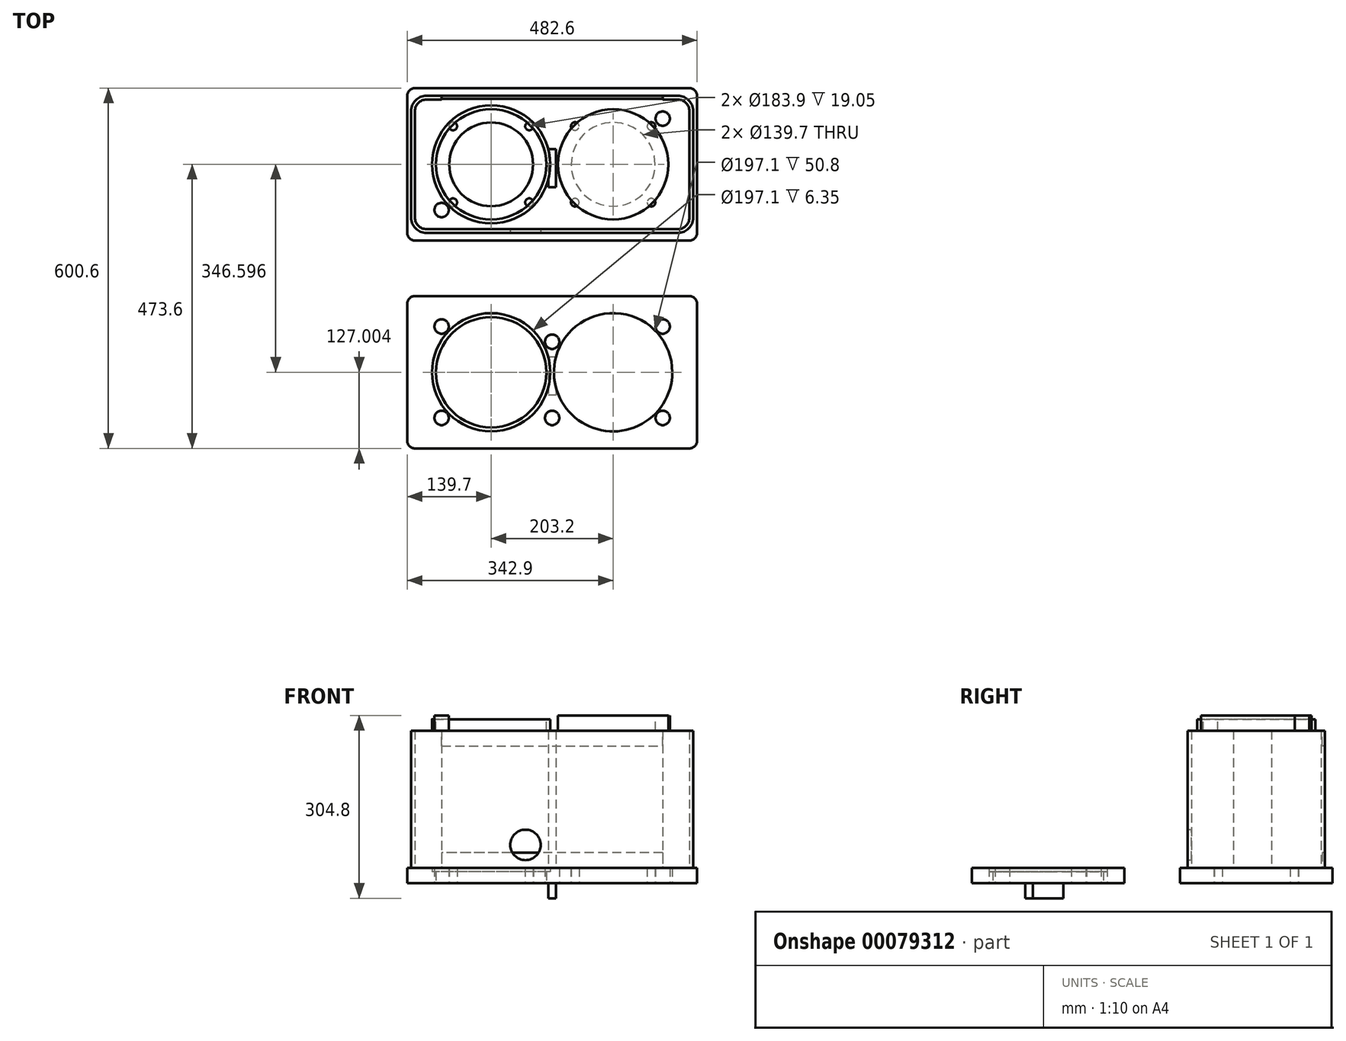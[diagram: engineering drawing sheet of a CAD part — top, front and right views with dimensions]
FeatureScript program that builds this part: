
annotation { "Feature Type Name" : "Feature", "Feature Type Description" : "" }
export const myFeature = defineFeature(function(context is Context, id is Id, definition is map)
    precondition{}
    {
        {
            var Q0;
            Q0=qCreatedBy(makeId("Top.planeOp"),FACE);
            var sketch = newSketch(context, id + "F0", { "sketchPlane" : qUnion([Q0])});
            skLineSegment(sketch, "E0.bottom", {"start": v(241.3, -127) * mm, "end": v(-241.3, -127) * mm});
            skLineSegment(sketch, "E0.top", {"start": v(241.3, 127) * mm, "end": v(-241.3, 127) * mm});
            skLineSegment(sketch, "E0.left", {"start": v(241.3, -127) * mm, "end": v(241.3, 127) * mm});
            skLineSegment(sketch, "E0.right", {"start": v(-241.3, -127) * mm, "end": v(-241.3, 127) * mm});
            skPoint(sketch, "E0.middle", {"position": v(0, 0) * mm});
            skSolve(sketch);
        }
        {
            var Q0;
            Q0=makeQuery(id+"F0.imprint","IMPRINT",FACE,{"disambiguationData":[TD([[makeQuery(id+"F0.imprint","IMPRINT",EDGE,{"derivedFrom":sQuery(id+"F0.wireOp",EDGE,"E0.bottom")}),-1.0]])]});
            extrude(context, id + "F1", {"entities" : qUnion([Q0]), "depth" : 25.4 * mm});
        }
        {
            var Q0;
            Q0=makeQuery(id+"F1.opExtrude","CAP_FACE",FACE,{"disambiguationData":[OSD([sQuery(id+"F0.wireOp",EDGE,"E0.bottom"),sQuery(id+"F0.wireOp",EDGE,"E0.top"),sQuery(id+"F0.wireOp",EDGE,"E0.left"),sQuery(id+"F0.wireOp",EDGE,"E0.right")])],"isStart":false});
            var sketch = newSketch(context, id + "F2", { "sketchPlane" : qUnion([Q0])});
            skLineSegment(sketch, "E1.bottom", {"start": v(209.55, -114.3) * mm, "end": v(-209.55, -114.3) * mm});
            skLineSegment(sketch, "E1.left", {"start": v(234.95, -88.9) * mm, "end": v(234.95, 88.9) * mm});
            skLineSegment(sketch, "E1.right", {"start": v(-234.95, -88.9) * mm, "end": v(-234.95, 88.9) * mm});
            skPoint(sketch, "E1.middle", {"position": v(0, 0) * mm});
            skLineSegment(sketch, "E2.bottom", {"start": v(209.55, -107.95) * mm, "end": v(-209.55, -107.95) * mm});
            skLineSegment(sketch, "E2.left", {"start": v(228.6, -88.9) * mm, "end": v(228.6, 88.9) * mm});
            skLineSegment(sketch, "E2.right", {"start": v(-228.6, -88.9) * mm, "end": v(-228.6, 88.9) * mm});
            skLineSegment(sketch, "E3", {"start": v(-209.55, 114.3) * mm, "end": v(-184.15, 114.3) * mm});
            skLineSegment(sketch, "E4", {"start": v(-209.55, 107.95) * mm, "end": v(-184.14, 107.95) * mm});
            skLineSegment(sketch, "E5", {"start": v(-184.15, 114.3) * mm, "end": v(-184.14, 107.95) * mm});
            skLineSegment(sketch, "E6", {"start": v(209.55, 114.3) * mm, "end": v(184.15, 114.3) * mm});
            skLineSegment(sketch, "E7", {"start": v(184.15, 114.3) * mm, "end": v(184.15, 107.95) * mm});
            skLineSegment(sketch, "E8", {"start": v(184.15, 107.95) * mm, "end": v(209.55, 107.95) * mm});
            skPoint(sketch, "E9.visualSharp", {"position": v(-234.95, 114.3) * mm});
            skArc(sketch, "E9.filletArc", {"start": v(-209.55, 114.3) * mm, "mid": v(-227.51, 106.86) * mm, "end": v(-234.95, 88.9) * mm});
            skPoint(sketch, "E10.visualSharp", {"position": v(-234.95, -114.3) * mm});
            skArc(sketch, "E10.filletArc", {"start": v(-234.95, -88.9) * mm, "mid": v(-227.51, -106.86) * mm, "end": v(-209.55, -114.3) * mm});
            skPoint(sketch, "E11.visualSharp", {"position": v(234.95, -114.3) * mm});
            skArc(sketch, "E11.filletArc", {"start": v(209.55, -114.3) * mm, "mid": v(227.51, -106.86) * mm, "end": v(234.95, -88.9) * mm});
            skPoint(sketch, "E12.visualSharp", {"position": v(234.95, 114.3) * mm});
            skArc(sketch, "E12.filletArc", {"start": v(234.95, 88.9) * mm, "mid": v(227.51, 106.86) * mm, "end": v(209.55, 114.3) * mm});
            skPoint(sketch, "E13.visualSharp", {"position": v(-228.6, 107.95) * mm});
            skArc(sketch, "E13.filletArc", {"start": v(-209.55, 107.95) * mm, "mid": v(-223.02, 102.37) * mm, "end": v(-228.6, 88.9) * mm});
            skPoint(sketch, "E14.visualSharp", {"position": v(-228.6, -107.95) * mm});
            skArc(sketch, "E14.filletArc", {"start": v(-228.6, -88.9) * mm, "mid": v(-223.02, -102.37) * mm, "end": v(-209.55, -107.95) * mm});
            skPoint(sketch, "E15.visualSharp", {"position": v(228.6, -107.95) * mm});
            skArc(sketch, "E15.filletArc", {"start": v(209.55, -107.95) * mm, "mid": v(223.02, -102.37) * mm, "end": v(228.6, -88.9) * mm});
            skPoint(sketch, "E16.visualSharp", {"position": v(228.6, 107.95) * mm});
            skArc(sketch, "E16.filletArc", {"start": v(228.6, 88.9) * mm, "mid": v(223.02, 102.37) * mm, "end": v(209.55, 107.95) * mm});
            skLineSegment(sketch, "E17.bottom", {"start": v(-6.35, 25.4) * mm, "end": v(6.35, 25.4) * mm});
            skLineSegment(sketch, "E17.top", {"start": v(-6.35, -38.1) * mm, "end": v(6.35, -38.1) * mm});
            skLineSegment(sketch, "E17.left", {"start": v(-6.35, 25.4) * mm, "end": v(-6.35, -38.1) * mm});
            skLineSegment(sketch, "E17.right", {"start": v(6.35, 25.4) * mm, "end": v(6.35, -38.1) * mm});
            skSolve(sketch);
        }
        {
            var Q0;
            Q0=makeQuery(id+"F2.imprint","IMPRINT",FACE,{"disambiguationData":[TD([[makeQuery(id+"F2.imprint","IMPRINT",EDGE,{"derivedFrom":sQuery(id+"F2.wireOp",EDGE,"E1.bottom")}),-1.0]])]});
            var Q1;
            Q1=makeQuery(id+"F2.imprint","IMPRINT",FACE,{"disambiguationData":[TD([[makeQuery(id+"F2.imprint","IMPRINT",EDGE,{"derivedFrom":sQuery(id+"F2.wireOp",EDGE,"E17.bottom")}),-1.0]])]});
            extrude(context, id + "F3", {"entities" : qUnion([Q0, Q1]), "operationType" : NewBodyOperationType.ADD, "depth" : 228.6 * mm});
        }
        {
            var Q0;
            Q0=makeQuery(id+"F3.opExtrude","CAP_FACE",FACE,{"disambiguationData":[OSD([sQuery(id+"F2.wireOp",EDGE,"E1.bottom"),sQuery(id+"F2.wireOp",EDGE,"E1.left"),sQuery(id+"F2.wireOp",EDGE,"E1.right"),sQuery(id+"F2.wireOp",EDGE,"E2.bottom"),sQuery(id+"F2.wireOp",EDGE,"E2.left"),sQuery(id+"F2.wireOp",EDGE,"E2.right"),sQuery(id+"F2.wireOp",EDGE,"E3"),sQuery(id+"F2.wireOp",EDGE,"E4"),sQuery(id+"F2.wireOp",EDGE,"E5"),sQuery(id+"F2.wireOp",EDGE,"E6"),sQuery(id+"F2.wireOp",EDGE,"E7"),sQuery(id+"F2.wireOp",EDGE,"E8"),sQuery(id+"F2.wireOp",EDGE,"E9.filletArc"),sQuery(id+"F2.wireOp",EDGE,"E10.filletArc"),sQuery(id+"F2.wireOp",EDGE,"E11.filletArc"),sQuery(id+"F2.wireOp",EDGE,"E12.filletArc"),sQuery(id+"F2.wireOp",EDGE,"E13.filletArc"),sQuery(id+"F2.wireOp",EDGE,"E14.filletArc"),sQuery(id+"F2.wireOp",EDGE,"E15.filletArc"),sQuery(id+"F2.wireOp",EDGE,"E16.filletArc")])],"isStart":false});
            var sketch = newSketch(context, id + "F4", { "sketchPlane" : qUnion([Q0])});
            skLineSegment(sketch, "E18.bottom", {"start": v(241.3, -127) * mm, "end": v(-241.3, -127) * mm});
            skLineSegment(sketch, "E18.top", {"start": v(241.3, 127) * mm, "end": v(-241.3, 127) * mm});
            skLineSegment(sketch, "E18.left", {"start": v(241.3, -127) * mm, "end": v(241.3, 127) * mm});
            skLineSegment(sketch, "E18.right", {"start": v(-241.3, -127) * mm, "end": v(-241.3, 127) * mm});
            skPoint(sketch, "E18.middle", {"position": v(0, 0) * mm});
            skSolve(sketch);
        }
        {
            var Q0;
            Q0=qSketchRegion(id+"F4",true);
            extrude(context, id + "F5", {"entities" : qUnion([Q0]), "operationType" : NewBodyOperationType.ADD, "depth" : 25.4 * mm});
        }
        {
            var Q0;
            Q0=makeQuery(id+"F3.opExtrude","SWEPT_FACE",FACE,{"disambiguationData":[OSD([sQuery(id+"F2.wireOp",EDGE,"E1.bottom")])]});
            var sketch = newSketch(context, id + "F6", { "sketchPlane" : qUnion([Q0])});
            skCircle(sketch, "E19", {"center": v(-44.45, 63.5) * mm, "radius": 25.4 * mm});
            skSolve(sketch);
        }
        {
            var Q0;
            Q0=makeQuery(id+"F6.imprint","IMPRINT",FACE,{"disambiguationData":[TD([[makeQuery(id+"F6.imprint","IMPRINT",EDGE,{"derivedFrom":sQuery(id+"F6.wireOp",EDGE,"E19")}),1.0]])]});
            extrude(context, id + "F7", {"entities" : qUnion([Q0]), "operationType" : NewBodyOperationType.REMOVE, "oppositeDirection" : true, "depth" : 6.35 * mm});
        }
        {
            var Q0;
            Q0=qCreatedBy(makeId("Right.planeOp"),FACE);
            var sketch = newSketch(context, id + "F8", { "sketchPlane" : qUnion([Q0])});
            skLineSegment(sketch, "E20", {"start": v(0, -47.78) * mm, "end": v(0, 307.42) * mm, "construction": true});
            skSolve(sketch);
        }
        {
            var Q0;
            Q0=makeQuery(id+"F5.opExtrude","CAP_FACE",FACE,{"disambiguationData":[OSD([sQuery(id+"F4.wireOp",EDGE,"E18.bottom"),sQuery(id+"F4.wireOp",EDGE,"E18.top"),sQuery(id+"F4.wireOp",EDGE,"E18.left"),sQuery(id+"F4.wireOp",EDGE,"E18.right")])],"isStart":false});
            var sketch = newSketch(context, id + "F9", { "sketchPlane" : qUnion([Q0])});
            skLineSegment(sketch, "E21", {"start": v(-271.52, 0) * mm, "end": v(283.67, 0) * mm, "construction": true});
            skLineSegment(sketch, "E22", {"start": v(0, 144.93) * mm, "end": v(0, -150.4) * mm, "construction": true});
            skPoint(sketch, "E22.endSnap0", {"position": v(0, -127) * mm});
            skCircle(sketch, "E23", {"center": v(-101.6, 0) * mm, "radius": 98.55 * mm});
            skCircle(sketch, "E24", {"center": v(-101.6, 0) * mm, "radius": 91.95 * mm});
            skCircle(sketch, "E25", {"center": v(-184.15, 76.2) * mm, "radius": 11.94 * mm});
            skCircle(sketch, "E26", {"center": v(0, 50.8) * mm, "radius": 11.94 * mm});
            skCircle(sketch, "E27", {"center": v(0, -76.2) * mm, "radius": 11.94 * mm});
            skCircle(sketch, "E28.MirrorC", {"center": v(101.6, 0) * mm, "radius": 98.55 * mm});
            skCircle(sketch, "E29.MirrorC", {"center": v(101.6, 0) * mm, "radius": 91.95 * mm});
            skCircle(sketch, "E30.MirrorC", {"center": v(184.15, 76.2) * mm, "radius": 11.94 * mm});
            skCircle(sketch, "E31.MirrorC", {"center": v(184.15, -76.2) * mm, "radius": 11.94 * mm});
            skCircle(sketch, "E32.MirrorC", {"center": v(-184.15, -76.2) * mm, "radius": 11.94 * mm});
            skSolve(sketch);
        }
        {
            var Q0;
            Q0=makeQuery(id+"F9.imprint","IMPRINT",FACE,{"disambiguationData":[TD([[makeQuery(id+"F9.imprint","IMPRINT",EDGE,{"derivedFrom":sQuery(id+"F9.wireOp",EDGE,"E24")}),1.0]])]});
            var Q1;
            Q1=makeQuery(id+"F9.imprint","IMPRINT",FACE,{"disambiguationData":[TD([[makeQuery(id+"F9.imprint","IMPRINT",EDGE,{"derivedFrom":sQuery(id+"F9.wireOp",EDGE,"E29.MirrorC")}),-1.0]])]});
            var Q2;
            Q2=makeQuery(id+"F9.imprint","IMPRINT",FACE,{"disambiguationData":[TD([[makeQuery(id+"F9.imprint","IMPRINT",EDGE,{"derivedFrom":sQuery(id+"F9.wireOp",EDGE,"E30.MirrorC")}),-1.0]])]});
            var Q3;
            Q3=makeQuery(id+"F9.imprint","IMPRINT",FACE,{"disambiguationData":[TD([[makeQuery(id+"F9.imprint","IMPRINT",EDGE,{"derivedFrom":sQuery(id+"F9.wireOp",EDGE,"E31.MirrorC")}),1.0]])]});
            var Q4;
            Q4=makeQuery(id+"F9.imprint","IMPRINT",FACE,{"disambiguationData":[TD([[makeQuery(id+"F9.imprint","IMPRINT",EDGE,{"derivedFrom":sQuery(id+"F9.wireOp",EDGE,"E27")}),1.0]])]});
            var Q5;
            Q5=makeQuery(id+"F9.imprint","IMPRINT",FACE,{"disambiguationData":[TD([[makeQuery(id+"F9.imprint","IMPRINT",EDGE,{"derivedFrom":sQuery(id+"F9.wireOp",EDGE,"E26")}),1.0]])]});
            var Q6;
            Q6=makeQuery(id+"F9.imprint","IMPRINT",FACE,{"disambiguationData":[TD([[makeQuery(id+"F9.imprint","IMPRINT",EDGE,{"derivedFrom":sQuery(id+"F9.wireOp",EDGE,"E25")}),1.0]])]});
            var Q7;
            Q7=makeQuery(id+"F9.imprint","IMPRINT",FACE,{"disambiguationData":[TD([[makeQuery(id+"F9.imprint","IMPRINT",EDGE,{"derivedFrom":sQuery(id+"F9.wireOp",EDGE,"E32.MirrorC")}),-1.0]])]});
            extrude(context, id + "F10", {"entities" : qUnion([Q0, Q1, Q2, Q3, Q4, Q5, Q6, Q7]), "operationType" : NewBodyOperationType.REMOVE, "oppositeDirection" : true, "depth" : 25.4 * mm});
        }
        {
            var Q0;
            Q0=makeQuery(id+"F9.imprint","IMPRINT",FACE,{"disambiguationData":[TD([[makeQuery(id+"F9.imprint","IMPRINT",EDGE,{"derivedFrom":sQuery(id+"F9.wireOp",EDGE,"E23")}),1.0]])]});
            var Q1;
            Q1=makeQuery(id+"F9.imprint","IMPRINT",FACE,{"disambiguationData":[TD([[makeQuery(id+"F9.imprint","IMPRINT",EDGE,{"derivedFrom":sQuery(id+"F9.wireOp",EDGE,"E28.MirrorC")}),-1.0]])]});
            extrude(context, id + "F11", {"entities" : qUnion([Q0, Q1]), "operationType" : NewBodyOperationType.REMOVE, "oppositeDirection" : true, "depth" : 6.35 * mm});
        }
        {
            var Q0;
            Q0=makeQuery(id+"F1.opExtrude","CAP_FACE",FACE,{"disambiguationData":[OSD([sQuery(id+"F0.wireOp",EDGE,"E0.bottom"),sQuery(id+"F0.wireOp",EDGE,"E0.top"),sQuery(id+"F0.wireOp",EDGE,"E0.left"),sQuery(id+"F0.wireOp",EDGE,"E0.right")])],"isStart":true});
            var sketch = newSketch(context, id + "F12", { "sketchPlane" : qUnion([Q0])});
            skLineSegment(sketch, "E33", {"start": v(292.64, 0) * mm, "end": v(-290.7, 0) * mm, "construction": true});
            skLineSegment(sketch, "E34", {"start": v(0, -152.7) * mm, "end": v(0, 157.85) * mm, "construction": true});
            skCircle(sketch, "E35", {"center": v(101.6, 0) * mm, "radius": 69.85 * mm});
            skLineSegment(sketch, "E36", {"start": v(101.6, 0) * mm, "end": v(165.1, -63.5) * mm, "construction": true});
            skCircle(sketch, "E37", {"center": v(165.1, -63.5) * mm, "radius": 6.75 * mm});
            skCircle(sketch, "E38.1.0", {"center": v(165.1, 63.5) * mm, "radius": 6.75 * mm});
            skCircle(sketch, "E38.2.0", {"center": v(38.1, 63.5) * mm, "radius": 6.75 * mm});
            skCircle(sketch, "E38.3.0", {"center": v(38.1, -63.5) * mm, "radius": 6.75 * mm});
            skCircle(sketch, "E39.MirrorC", {"center": v(-38.1, -63.5) * mm, "radius": 6.75 * mm});
            skCircle(sketch, "E40.MirrorC", {"center": v(-101.6, 0) * mm, "radius": 69.85 * mm});
            skCircle(sketch, "E41.MirrorC", {"center": v(-38.1, 63.5) * mm, "radius": 6.75 * mm});
            skCircle(sketch, "E42.MirrorC", {"center": v(-165.1, 63.5) * mm, "radius": 6.75 * mm});
            skCircle(sketch, "E43.MirrorC", {"center": v(-165.1, -63.5) * mm, "radius": 6.75 * mm});
            skSolve(sketch);
        }
        {
            var Q0;
            Q0 = qSketchRegion(id + "F12", true);
            extrude(context, id + "F13", {"entities" : qUnion([Q0]), "operationType" : NewBodyOperationType.REMOVE, "oppositeDirection" : true, "depth" : 25.4 * mm});
        }
        {
            var Q0;
            Q0=makeQuery(id+"F1.opExtrude","CAP_FACE",FACE,{"disambiguationData":[OSD([sQuery(id+"F0.wireOp",EDGE,"E0.bottom"),sQuery(id+"F0.wireOp",EDGE,"E0.top"),sQuery(id+"F0.wireOp",EDGE,"E0.left"),sQuery(id+"F0.wireOp",EDGE,"E0.right")])],"isStart":false});
            var sketch = newSketch(context, id + "F14", { "sketchPlane" : qUnion([Q0])});
            skLineSegment(sketch, "E44.bottom", {"start": v(184.15, 109.54) * mm, "end": v(-184.15, 109.54) * mm});
            skLineSegment(sketch, "E44.top", {"start": v(184.15, 114.3) * mm, "end": v(-184.15, 114.3) * mm});
            skLineSegment(sketch, "E44.left", {"start": v(184.15, 109.54) * mm, "end": v(184.15, 114.3) * mm});
            skLineSegment(sketch, "E44.right", {"start": v(-184.15, 109.54) * mm, "end": v(-184.15, 114.3) * mm});
            skPoint(sketch, "E44.middle", {"position": v(0, 111.92) * mm});
            skSolve(sketch);
        }
        {
            var Q0;
            {var subQ4=sQuery(id+"F14.wireOp",EDGE,"E44.top");Q0=makeQuery(id+"F14.imprint","IMPRINT",FACE,{"disambiguationData":[TD([[makeQuery(id+"F14.imprint","IMPRINT",EDGE,{"derivedFrom":subQ4}),1.0]])]});}
            extrude(context, id + "F15", {"entities" : qUnion([Q0]), "depth" : 25.4 * mm});
        }
        {
            var Q0;
            Q0=makeQuery(id+"F5.opExtrude","CAP_FACE",FACE,{"disambiguationData":[OSD([sQuery(id+"F4.wireOp",EDGE,"E18.bottom"),sQuery(id+"F4.wireOp",EDGE,"E18.top"),sQuery(id+"F4.wireOp",EDGE,"E18.left"),sQuery(id+"F4.wireOp",EDGE,"E18.right")])],"isStart":true});
            var sketch = newSketch(context, id + "F16", { "sketchPlane" : qUnion([Q0])});
            skLineSegment(sketch, "E45.bottom", {"start": v(-184.15, -114.3) * mm, "end": v(184.15, -114.3) * mm});
            skLineSegment(sketch, "E45.top", {"start": v(-184.15, -109.54) * mm, "end": v(184.15, -109.54) * mm});
            skLineSegment(sketch, "E45.left", {"start": v(-184.15, -114.3) * mm, "end": v(-184.15, -109.54) * mm});
            skLineSegment(sketch, "E45.right", {"start": v(184.15, -114.3) * mm, "end": v(184.15, -109.54) * mm});
            skPoint(sketch, "E45.middle", {"position": v(0, -111.92) * mm});
            skSolve(sketch);
        }
        {
            var Q0;
            {var subQ0=sQuery(id+"F16.wireOp",EDGE,"E45.bottom");Q0=makeQuery(id+"F16.imprint","IMPRINT",FACE,{"disambiguationData":[TD([[makeQuery(id+"F16.imprint","IMPRINT",EDGE,{"derivedFrom":subQ0}),1.0]])]});}
            extrude(context, id + "F17", {"entities" : qUnion([Q0]), "depth" : 25.4 * mm});
        }
        {
            var Q0;
            Q0=qCreatedBy(makeId("Top.planeOp"),FACE);
            var sketch = newSketch(context, id + "F18", { "sketchPlane" : qUnion([Q0])});
            skLineSegment(sketch, "E46.bottom", {"start": v(241.3, -219.6) * mm, "end": v(-241.3, -219.6) * mm});
            skLineSegment(sketch, "E46.top", {"start": v(241.3, -473.6) * mm, "end": v(-241.3, -473.6) * mm});
            skLineSegment(sketch, "E46.left", {"start": v(241.3, -219.6) * mm, "end": v(241.3, -473.6) * mm});
            skLineSegment(sketch, "E46.right", {"start": v(-241.3, -219.6) * mm, "end": v(-241.3, -473.6) * mm});
            skPoint(sketch, "E46.middle", {"position": v(0, -346.6) * mm});
            skLineSegment(sketch, "E47", {"start": v(-271.52, -346.6) * mm, "end": v(283.67, -346.6) * mm, "construction": true});
            skLineSegment(sketch, "E48", {"start": v(0, -187.96) * mm, "end": v(0, -483.28) * mm, "construction": true});
            skPoint(sketch, "E48.endSnap0", {"position": v(0, -459.89) * mm});
            skCircle(sketch, "E49", {"center": v(-101.6, -346.6) * mm, "radius": 98.55 * mm});
            skCircle(sketch, "E50", {"center": v(-101.6, -346.6) * mm, "radius": 91.95 * mm});
            skCircle(sketch, "E51", {"center": v(-184.15, -270.4) * mm, "radius": 11.94 * mm});
            skCircle(sketch, "E52", {"center": v(0, -295.8) * mm, "radius": 11.94 * mm});
            skCircle(sketch, "E53", {"center": v(0, -422.8) * mm, "radius": 11.94 * mm});
            skCircle(sketch, "E54.MirrorC", {"center": v(101.6, -346.6) * mm, "radius": 98.55 * mm});
            skCircle(sketch, "E55.MirrorC", {"center": v(101.6, -346.6) * mm, "radius": 91.95 * mm});
            skCircle(sketch, "E56.MirrorC", {"center": v(184.15, -270.4) * mm, "radius": 11.94 * mm});
            skCircle(sketch, "E57.MirrorC", {"center": v(184.15, -422.8) * mm, "radius": 11.94 * mm});
            skCircle(sketch, "E58.MirrorC", {"center": v(-184.15, -422.8) * mm, "radius": 11.94 * mm});
            skSolve(sketch);
        }
        {
            var Q0;
            Q0=makeQuery(id+"F18.imprint","IMPRINT",FACE,{"disambiguationData":[TD([[makeQuery(id+"F18.imprint","IMPRINT",EDGE,{"derivedFrom":sQuery(id+"F18.wireOp",EDGE,"E46.bottom")}),1.0]])]});
            extrude(context, id + "F19", {"entities" : qUnion([Q0]), "depth" : 25.4 * mm});
        }
        {
            var Q0;
            Q0=makeQuery(id+"F18.imprint","IMPRINT",FACE,{"disambiguationData":[TD([[makeQuery(id+"F18.imprint","IMPRINT",EDGE,{"derivedFrom":sQuery(id+"F18.wireOp",EDGE,"E49")}),1.0]])]});
            var Q1;
            Q1=makeQuery(id+"F18.imprint","IMPRINT",FACE,{"disambiguationData":[TD([[makeQuery(id+"F18.imprint","IMPRINT",EDGE,{"derivedFrom":sQuery(id+"F18.wireOp",EDGE,"E54.MirrorC")}),-1.0]])]});
            extrude(context, id + "F20", {"entities" : qUnion([Q0, Q1]), "operationType" : NewBodyOperationType.ADD, "depth" : 19.05 * mm});
        }
        {
            var Q0;
            {var subQ0=sQuery(id+"F18.wireOp",EDGE,"E54.MirrorC");var subQ1=sQuery(id+"F18.wireOp",EDGE,"E49");Q0=makeQuery(id+"F20.boolean.opBoolean","MERGE",FACE,{"derivedFrom":[makeQuery(id+"F19.opExtrude","CAP_FACE",FACE,{"disambiguationData":[OSD([sQuery(id+"F18.wireOp",EDGE,"E46.bottom"),sQuery(id+"F18.wireOp",EDGE,"E46.top"),sQuery(id+"F18.wireOp",EDGE,"E46.left"),sQuery(id+"F18.wireOp",EDGE,"E46.right"),subQ1,sQuery(id+"F18.wireOp",EDGE,"E51"),sQuery(id+"F18.wireOp",EDGE,"E52"),sQuery(id+"F18.wireOp",EDGE,"E53"),subQ0,sQuery(id+"F18.wireOp",EDGE,"E56.MirrorC"),sQuery(id+"F18.wireOp",EDGE,"E57.MirrorC"),sQuery(id+"F18.wireOp",EDGE,"E58.MirrorC")])],"isStart":true}),makeQuery(id+"F20.opExtrude","CAP_FACE",FACE,{"disambiguationData":[OSD([subQ1,sQuery(id+"F18.wireOp",EDGE,"E50")])],"isStart":true}),makeQuery(id+"F20.opExtrude","CAP_FACE",FACE,{"disambiguationData":[OSD([subQ0,sQuery(id+"F18.wireOp",EDGE,"E55.MirrorC")])],"isStart":true})]});}
            var sketch = newSketch(context, id + "F21", { "sketchPlane" : qUnion([Q0])});
            skLineSegment(sketch, "E59.bottom", {"start": v(6.35, 321.2) * mm, "end": v(-6.35, 321.2) * mm});
            skLineSegment(sketch, "E59.top", {"start": v(6.35, 384.7) * mm, "end": v(-6.35, 384.7) * mm});
            skLineSegment(sketch, "E59.left", {"start": v(6.35, 321.2) * mm, "end": v(6.35, 384.7) * mm});
            skLineSegment(sketch, "E59.right", {"start": v(-6.35, 321.2) * mm, "end": v(-6.35, 384.7) * mm});
            skPoint(sketch, "E59.middle", {"position": v(0, 352.95) * mm});
            skSolve(sketch);
        }
        {
            var Q0;
            Q0=makeQuery(id+"F21.imprint","IMPRINT",FACE,{"disambiguationData":[TD([[makeQuery(id+"F21.imprint","IMPRINT",EDGE,{"derivedFrom":sQuery(id+"F21.wireOp",EDGE,"E59.bottom")}),-1.0]])]});
            extrude(context, id + "F22", {"entities" : qUnion([Q0]), "operationType" : NewBodyOperationType.ADD, "depth" : 25.4 * mm});
        }
        {
            var Q0;
            Q0=makeQuery(id+"F5.opExtrude","SWEPT_EDGE",EDGE,{"disambiguationData":[OSD([sQuery(id+"F4.wireOp",EDGE,"E18.bottom"),sQuery(id+"F4.wireOp",EDGE,"E18.left")])]});
            var Q1;
            Q1=makeQuery(id+"F5.opExtrude","SWEPT_EDGE",EDGE,{"disambiguationData":[OSD([sQuery(id+"F4.wireOp",EDGE,"E18.top"),sQuery(id+"F4.wireOp",EDGE,"E18.left")])]});
            var Q2;
            Q2=makeQuery(id+"F1.opExtrude","SWEPT_EDGE",EDGE,{"disambiguationData":[OSD([sQuery(id+"F0.wireOp",EDGE,"E0.top"),sQuery(id+"F0.wireOp",EDGE,"E0.left")])]});
            var Q3;
            Q3=makeQuery(id+"F1.opExtrude","SWEPT_EDGE",EDGE,{"disambiguationData":[OSD([sQuery(id+"F0.wireOp",EDGE,"E0.bottom"),sQuery(id+"F0.wireOp",EDGE,"E0.left")])]});
            var Q4;
            Q4=makeQuery(id+"F5.opExtrude","SWEPT_EDGE",EDGE,{"disambiguationData":[OSD([sQuery(id+"F4.wireOp",EDGE,"E18.bottom"),sQuery(id+"F4.wireOp",EDGE,"E18.right")])]});
            var Q5;
            Q5=makeQuery(id+"F1.opExtrude","SWEPT_EDGE",EDGE,{"disambiguationData":[OSD([sQuery(id+"F0.wireOp",EDGE,"E0.bottom"),sQuery(id+"F0.wireOp",EDGE,"E0.right")])]});
            var Q6;
            Q6=makeQuery(id+"F19.opExtrude","SWEPT_EDGE",EDGE,{"disambiguationData":[OSD([sQuery(id+"F18.wireOp",EDGE,"E46.bottom"),sQuery(id+"F18.wireOp",EDGE,"E46.left")])]});
            var Q7;
            Q7=makeQuery(id+"F19.opExtrude","SWEPT_EDGE",EDGE,{"disambiguationData":[OSD([sQuery(id+"F18.wireOp",EDGE,"E46.top"),sQuery(id+"F18.wireOp",EDGE,"E46.left")])]});
            var Q8;
            Q8=makeQuery(id+"F19.opExtrude","SWEPT_EDGE",EDGE,{"disambiguationData":[OSD([sQuery(id+"F18.wireOp",EDGE,"E46.top"),sQuery(id+"F18.wireOp",EDGE,"E46.right")])]});
            var Q9;
            Q9=makeQuery(id+"F5.opExtrude","SWEPT_EDGE",EDGE,{"disambiguationData":[OSD([sQuery(id+"F4.wireOp",EDGE,"E18.top"),sQuery(id+"F4.wireOp",EDGE,"E18.right")])]});
            var Q10;
            Q10=makeQuery(id+"F1.opExtrude","SWEPT_EDGE",EDGE,{"disambiguationData":[OSD([sQuery(id+"F0.wireOp",EDGE,"E0.top"),sQuery(id+"F0.wireOp",EDGE,"E0.right")])]});
            var Q11;
            Q11=makeQuery(id+"F19.opExtrude","SWEPT_EDGE",EDGE,{"disambiguationData":[OSD([sQuery(id+"F18.wireOp",EDGE,"E46.bottom"),sQuery(id+"F18.wireOp",EDGE,"E46.right")])]});
            fillet(context, id + "F23", {"entities" : qUnion([Q0, Q1, Q2, Q3, Q4, Q5, Q6, Q7, Q8, Q9, Q10, Q11]), "radius" : 12.7 * mm, "tangentPropagation" : true, "allowEdgeOverflow" : false});
        }
    });
